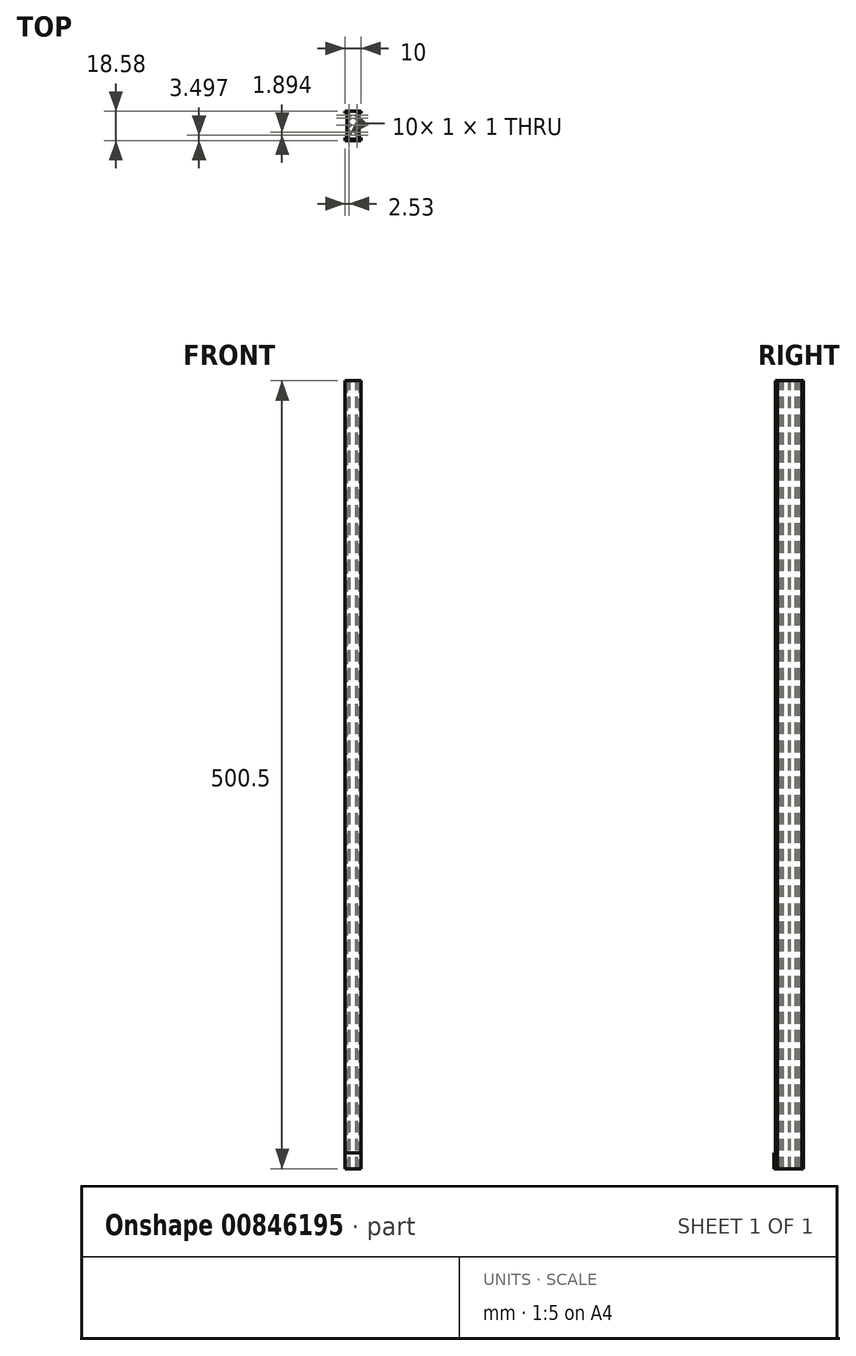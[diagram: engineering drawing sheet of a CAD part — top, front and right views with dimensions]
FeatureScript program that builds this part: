
annotation { "Feature Type Name" : "Feature", "Feature Type Description" : "" }
export const myFeature = defineFeature(function(context is Context, id is Id, definition is map)
    precondition{}
    {
        {
            var Q0;
            Q0=qCreatedBy(makeId("Top.planeOp"),FACE);
            var sketch = newSketch(context, id + "F0", { "sketchPlane" : qUnion([Q0])});
            skLineSegment(sketch, "E0", {"start": v(-5, 15.44) * mm, "end": v(5, 15.44) * mm});
            skLineSegment(sketch, "E1", {"start": v(5, 15.44) * mm, "end": v(5, 14.44) * mm});
            skLineSegment(sketch, "E2", {"start": v(-5, 15.44) * mm, "end": v(-5, 14.44) * mm});
            skLineSegment(sketch, "E3", {"start": v(-5, 14.44) * mm, "end": v(-3.67, 14.44) * mm});
            skLineSegment(sketch, "E4", {"start": v(5, 14.44) * mm, "end": v(3.67, 14.44) * mm});
            skLineSegment(sketch, "E5", {"start": v(-3.67, 14.44) * mm, "end": v(-3.67, -1.14) * mm});
            skLineSegment(sketch, "E6", {"start": v(3.67, 14.44) * mm, "end": v(3.67, -1.14) * mm});
            skLineSegment(sketch, "E7", {"start": v(-3.67, -1.14) * mm, "end": v(-5, -1.14) * mm});
            skLineSegment(sketch, "E8", {"start": v(3.67, -1.14) * mm, "end": v(5, -1.14) * mm});
            skLineSegment(sketch, "E9", {"start": v(-5, -1.14) * mm, "end": v(-5, -2.14) * mm});
            skLineSegment(sketch, "E10", {"start": v(5, -1.14) * mm, "end": v(5, -2.14) * mm});
            skLineSegment(sketch, "E11", {"start": v(-5, -2.14) * mm, "end": v(5, -2.14) * mm});
            skSolve(sketch);
        }
        {
            var Q0;
            Q0=makeQuery(id+"F0.imprint","IMPRINT",FACE,{"disambiguationData":[TD([[makeQuery(id+"F0.imprint","IMPRINT",EDGE,{"derivedFrom":sQuery(id+"F0.wireOp",EDGE,"E0")}),-1.0]])]});
            extrude(context, id + "F1", {"entities" : qUnion([Q0]), "depth" : 500.5 * mm, "offsetDistance" : 25 * mm});
        }
        {
            var Q0;
            Q0=makeQuery(id+"F1.opExtrude","SWEPT_FACE",FACE,{"disambiguationData":[OSD([sQuery(id+"F0.wireOp",EDGE,"E11")])]});
            var sketch = newSketch(context, id + "F2", { "sketchPlane" : qUnion([Q0])});
            skLineSegment(sketch, "E12", {"start": v(-5, 0) * mm, "end": v(5, 0) * mm});
            skLineSegment(sketch, "E13", {"start": v(5, 0) * mm, "end": v(5, 10) * mm});
            skLineSegment(sketch, "E14", {"start": v(5, 10) * mm, "end": v(-5, 10) * mm});
            skLineSegment(sketch, "E15", {"start": v(-5, 10) * mm, "end": v(-5, 0) * mm});
            skSolve(sketch);
        }
        {
            var Q0;
            Q0=makeQuery(id+"F2.imprint","IMPRINT",FACE,{"disambiguationData":[TD([[makeQuery(id+"F2.imprint","IMPRINT",EDGE,{"derivedFrom":sQuery(id+"F2.wireOp",EDGE,"E12")}),1.0]])]});
            extrude(context, id + "F3", {"entities" : qUnion([Q0]), "operationType" : NewBodyOperationType.ADD, "depth" : 1 * mm, "offsetDistance" : 25 * mm});
        }
        {
            var Q0;
            Q0=makeQuery(id+"F1.opExtrude","CAP_FACE",FACE,{"disambiguationData":[OSD([sQuery(id+"F0.wireOp",EDGE,"E0"),sQuery(id+"F0.wireOp",EDGE,"E1"),sQuery(id+"F0.wireOp",EDGE,"E2"),sQuery(id+"F0.wireOp",EDGE,"E3"),sQuery(id+"F0.wireOp",EDGE,"E4"),sQuery(id+"F0.wireOp",EDGE,"E5"),sQuery(id+"F0.wireOp",EDGE,"E6"),sQuery(id+"F0.wireOp",EDGE,"E7"),sQuery(id+"F0.wireOp",EDGE,"E8"),sQuery(id+"F0.wireOp",EDGE,"E9"),sQuery(id+"F0.wireOp",EDGE,"E10"),sQuery(id+"F0.wireOp",EDGE,"E11")])],"isStart":false});
            var sketch = newSketch(context, id + "F4", { "sketchPlane" : qUnion([Q0])});
            skLineSegment(sketch, "E16", {"start": v(0, -4.4) * mm, "end": v(0, 15.78) * mm});
            skPoint(sketch, "E16.startSnap0", {"position": v(0, 15.44) * mm});
            skLineSegment(sketch, "E17", {"start": v(-2.97, 13.44) * mm, "end": v(-2.97, 12.44) * mm});
            skLineSegment(sketch, "E18", {"start": v(-2.97, 13.44) * mm, "end": v(-1.97, 13.44) * mm});
            skLineSegment(sketch, "E19", {"start": v(-1.97, 13.44) * mm, "end": v(-1.97, 12.44) * mm});
            skLineSegment(sketch, "E20", {"start": v(-2.97, 12.44) * mm, "end": v(-1.97, 12.44) * mm});
            skLineSegment(sketch, "E21.MirrorCS", {"start": v(1.97, 13.44) * mm, "end": v(1.97, 12.44) * mm});
            skLineSegment(sketch, "E22.MirrorCS", {"start": v(2.97, 13.44) * mm, "end": v(2.97, 12.44) * mm});
            skLineSegment(sketch, "E23.MirrorCS", {"start": v(2.97, 13.44) * mm, "end": v(1.97, 13.44) * mm});
            skLineSegment(sketch, "E24.MirrorCS", {"start": v(2.97, 12.44) * mm, "end": v(1.97, 12.44) * mm});
            skPoint(sketch, "E25", {"position": v(-2.97, -0.14) * mm});
            skLineSegment(sketch, "E26", {"start": v(-2.97, -0.14) * mm, "end": v(-2.97, 0.86) * mm});
            skLineSegment(sketch, "E27", {"start": v(-2.97, 0.86) * mm, "end": v(-1.97, 0.86) * mm});
            skLineSegment(sketch, "E28", {"start": v(-1.97, 0.86) * mm, "end": v(-1.97, -0.14) * mm});
            skLineSegment(sketch, "E29", {"start": v(-2.97, -0.14) * mm, "end": v(-1.97, -0.14) * mm});
            skLineSegment(sketch, "E30.MirrorCS", {"start": v(2.97, 0.86) * mm, "end": v(1.97, 0.86) * mm});
            skLineSegment(sketch, "E31.MirrorCS", {"start": v(2.97, -0.14) * mm, "end": v(1.97, -0.14) * mm});
            skLineSegment(sketch, "E32.MirrorCS", {"start": v(2.97, -0.14) * mm, "end": v(2.97, 0.86) * mm});
            skLineSegment(sketch, "E33.MirrorCS", {"start": v(1.97, 0.86) * mm, "end": v(1.97, -0.14) * mm});
            skLineSegment(sketch, "E34", {"start": v(-2.97, 7.18) * mm, "end": v(-1.97, 7.18) * mm});
            skLineSegment(sketch, "E35", {"start": v(-2.97, 7.18) * mm, "end": v(-2.97, 6.18) * mm});
            skLineSegment(sketch, "E36", {"start": v(-2.97, 6.18) * mm, "end": v(-1.97, 6.18) * mm});
            skLineSegment(sketch, "E37", {"start": v(-1.97, 7.18) * mm, "end": v(-1.97, 6.18) * mm});
            skLineSegment(sketch, "E38.MirrorCS", {"start": v(2.97, 7.18) * mm, "end": v(1.97, 7.18) * mm});
            skLineSegment(sketch, "E39.MirrorCS", {"start": v(2.97, 7.18) * mm, "end": v(2.97, 6.18) * mm});
            skLineSegment(sketch, "E40.MirrorCS", {"start": v(1.97, 7.18) * mm, "end": v(1.97, 6.18) * mm});
            skLineSegment(sketch, "E41.MirrorCS", {"start": v(2.97, 6.18) * mm, "end": v(1.97, 6.18) * mm});
            skLineSegment(sketch, "E42", {"start": v(-2.97, 11.54) * mm, "end": v(-1.97, 11.54) * mm});
            skPoint(sketch, "E42.endSnap0", {"position": v(-1.97, 12.94) * mm});
            skLineSegment(sketch, "E43", {"start": v(-2.97, 11.54) * mm, "end": v(-2.97, 10.54) * mm});
            skLineSegment(sketch, "E44", {"start": v(-2.97, 10.54) * mm, "end": v(-1.97, 10.54) * mm});
            skLineSegment(sketch, "E45", {"start": v(-1.97, 11.54) * mm, "end": v(-1.97, 10.54) * mm});
            skLineSegment(sketch, "E46.MirrorCS", {"start": v(1.97, 11.54) * mm, "end": v(1.97, 10.54) * mm});
            skLineSegment(sketch, "E47.MirrorCS", {"start": v(2.97, 11.54) * mm, "end": v(2.97, 10.54) * mm});
            skLineSegment(sketch, "E48.MirrorCS", {"start": v(2.97, 11.54) * mm, "end": v(1.97, 11.54) * mm});
            skLineSegment(sketch, "E49.MirrorCS", {"start": v(2.97, 10.54) * mm, "end": v(1.97, 10.54) * mm});
            skPoint(sketch, "E50", {"position": v(-2.97, 1.75) * mm});
            skLineSegment(sketch, "E51", {"start": v(-2.97, 1.75) * mm, "end": v(-2.97, 2.75) * mm});
            skLineSegment(sketch, "E52", {"start": v(-2.97, 2.75) * mm, "end": v(-1.97, 2.75) * mm});
            skLineSegment(sketch, "E53", {"start": v(-1.97, 2.75) * mm, "end": v(-1.97, 1.75) * mm});
            skLineSegment(sketch, "E54", {"start": v(-2.97, 1.75) * mm, "end": v(-1.97, 1.75) * mm});
            skLineSegment(sketch, "E55.MirrorCS", {"start": v(1.97, 2.75) * mm, "end": v(1.97, 1.75) * mm});
            skLineSegment(sketch, "E56.MirrorCS", {"start": v(2.97, 1.75) * mm, "end": v(2.97, 2.75) * mm});
            skLineSegment(sketch, "E57.MirrorCS", {"start": v(2.97, 1.75) * mm, "end": v(1.97, 1.75) * mm});
            skLineSegment(sketch, "E58.MirrorCS", {"start": v(2.97, 2.75) * mm, "end": v(1.97, 2.75) * mm});
            skSolve(sketch);
        }
        {
            var Q0;
            Q0=makeQuery(id+"F4.imprint","IMPRINT",FACE,{"disambiguationData":[TD([[makeQuery(id+"F4.imprint","IMPRINT",EDGE,{"derivedFrom":sQuery(id+"F4.wireOp",EDGE,"E17")}),1.0]])]});
            var Q1;
            Q1=makeQuery(id+"F4.imprint","IMPRINT",FACE,{"disambiguationData":[TD([[makeQuery(id+"F4.imprint","IMPRINT",EDGE,{"derivedFrom":sQuery(id+"F4.wireOp",EDGE,"E26")}),-1.0]])]});
            var Q2;
            Q2=makeQuery(id+"F4.imprint","IMPRINT",FACE,{"disambiguationData":[TD([[makeQuery(id+"F4.imprint","IMPRINT",EDGE,{"derivedFrom":sQuery(id+"F4.wireOp",EDGE,"E21.MirrorCS")}),1.0]])]});
            var Q3;
            Q3=makeQuery(id+"F4.imprint","IMPRINT",FACE,{"disambiguationData":[TD([[makeQuery(id+"F4.imprint","IMPRINT",EDGE,{"derivedFrom":sQuery(id+"F4.wireOp",EDGE,"E30.MirrorCS")}),1.0]])]});
            var Q4;
            Q4=makeQuery(id+"F4.imprint","IMPRINT",FACE,{"disambiguationData":[TD([[makeQuery(id+"F4.imprint","IMPRINT",EDGE,{"derivedFrom":sQuery(id+"F4.wireOp",EDGE,"E34")}),-1.0]])]});
            var Q5;
            Q5=makeQuery(id+"F4.imprint","IMPRINT",FACE,{"disambiguationData":[TD([[makeQuery(id+"F4.imprint","IMPRINT",EDGE,{"derivedFrom":sQuery(id+"F4.wireOp",EDGE,"E38.MirrorCS")}),1.0]])]});
            var Q6;
            Q6=makeQuery(id+"F4.imprint","IMPRINT",FACE,{"disambiguationData":[TD([[makeQuery(id+"F4.imprint","IMPRINT",EDGE,{"derivedFrom":sQuery(id+"F4.wireOp",EDGE,"E42")}),-1.0]])]});
            var Q7;
            Q7=makeQuery(id+"F4.imprint","IMPRINT",FACE,{"disambiguationData":[TD([[makeQuery(id+"F4.imprint","IMPRINT",EDGE,{"derivedFrom":sQuery(id+"F4.wireOp",EDGE,"E46.MirrorCS")}),1.0]])]});
            var Q8;
            Q8=makeQuery(id+"F4.imprint","IMPRINT",FACE,{"disambiguationData":[TD([[makeQuery(id+"F4.imprint","IMPRINT",EDGE,{"derivedFrom":sQuery(id+"F4.wireOp",EDGE,"E51")}),-1.0]])]});
            var Q9;
            Q9=makeQuery(id+"F4.imprint","IMPRINT",FACE,{"disambiguationData":[TD([[makeQuery(id+"F4.imprint","IMPRINT",EDGE,{"derivedFrom":sQuery(id+"F4.wireOp",EDGE,"E55.MirrorCS")}),1.0]])]});
            extrude(context, id + "F5", {"entities" : qUnion([Q0, Q1, Q2, Q3, Q4, Q5, Q6, Q7, Q8, Q9]), "operationType" : NewBodyOperationType.REMOVE, "oppositeDirection" : true, "depth" : 505.5 * mm, "offsetDistance" : 25 * mm});
        }
    });
